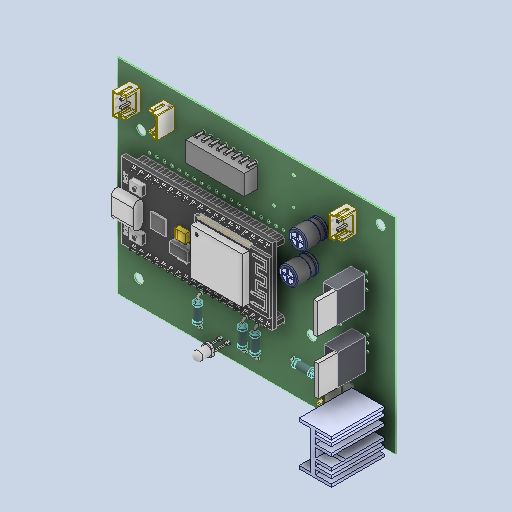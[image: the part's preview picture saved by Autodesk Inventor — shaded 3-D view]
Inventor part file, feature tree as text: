
AUTODESK INVENTOR PART (.ipt)
format: ipt  version: 2024 (Build 280153000, 153)  size: 6,783,488 bytes
history: native  units: in
note: dims shown in document units (in); Inventor stores cm internally (conversion verified against a paired STEP export)
features: other x145, extrude x53
ambient origin geometry x8: Origin, YZ Plane, XZ Plane, XY Plane, X Axis, Y Axis, Z Axis, Center Point
bodies: Solid1 (feature_tree), Solid2 (feature_tree), Solid3 (feature_tree), Solid4 (feature_tree), Solid5 (feature_tree), Solid6 (feature_tree), Solid7 (feature_tree), Solid8 (feature_tree), Solid9 (feature_tree), Solid10 (feature_tree), Solid11 (feature_tree), Solid12 (feature_tree), Solid13 (feature_tree), Solid14 (feature_tree), Solid15 (feature_tree), Solid16 (feature_tree), Solid17 (feature_tree), Solid18 (feature_tree), Solid19 (feature_tree), Solid20 (feature_tree), Solid21 (feature_tree), Solid22 (feature_tree), Solid23 (feature_tree), Solid24 (feature_tree), Solid25 (feature_tree), Solid26 (feature_tree), Solid27 (feature_tree), Solid28 (feature_tree), Solid29 (feature_tree), Solid30 (feature_tree), Solid31 (feature_tree), Solid32 (feature_tree), Solid33 (feature_tree), Solid34 (feature_tree), Solid35 (feature_tree), Solid36 (feature_tree), Solid37 (feature_tree), Solid38 (feature_tree), Solid39 (feature_tree), Solid40 (feature_tree), Solid41 (feature_tree), Solid42 (feature_tree), Solid43 (feature_tree), Solid44 (feature_tree), Solid45 (feature_tree), Solid46 (feature_tree), Solid47 (feature_tree), Solid48 (feature_tree), Solid49 (feature_tree), Solid50 (feature_tree), Solid51 (feature_tree), Solid52 (feature_tree), Solid53 (feature_tree), Solid54 (feature_tree), Solid55 (feature_tree), Solid56 (feature_tree), Solid57 (feature_tree), Solid58 (feature_tree), Solid59 (feature_tree), Solid60 (feature_tree), Solid61 (feature_tree), Solid62 (feature_tree), Solid63 (feature_tree), Solid64 (feature_tree), Solid65 (feature_tree), Solid66 (feature_tree), Solid67 (feature_tree), Solid68 (feature_tree), Solid69 (feature_tree), Solid70 (feature_tree), Solid71 (feature_tree), Solid72 (feature_tree), Solid73 (feature_tree), Solid74 (feature_tree), Solid75 (feature_tree), Solid76 (feature_tree), Solid77 (feature_tree), Solid78 (feature_tree), Solid79 (feature_tree), Solid80 (feature_tree), Solid81 (feature_tree), Solid82 (feature_tree), Solid83 (feature_tree), Solid84 (feature_tree), Solid85 (feature_tree), Solid86 (feature_tree), Solid87 (feature_tree), Solid88 (feature_tree), Solid89 (feature_tree), Solid90 (feature_tree), Solid91 (feature_tree), Solid92 (feature_tree), Solid93 (feature_tree), Solid94 (feature_tree), Solid95 (feature_tree), Solid96 (feature_tree), Solid97 (feature_tree), Solid98 (feature_tree), Solid99 (feature_tree), Solid100 (feature_tree), Solid101 (feature_tree), Solid102 (feature_tree), Solid103 (feature_tree), Solid104 (feature_tree), Solid105 (feature_tree), Solid106 (feature_tree), Solid107 (feature_tree), Solid108 (feature_tree), Solid109 (feature_tree), Solid110 (feature_tree), Solid111 (feature_tree), Solid112 (feature_tree), Solid113 (feature_tree), Solid114 (feature_tree), Solid115 (feature_tree), Solid116 (feature_tree), Solid117 (feature_tree), Solid118 (feature_tree), Solid119 (feature_tree), Solid120 (feature_tree), Solid121 (feature_tree), Solid122 (feature_tree), Solid123 (feature_tree), Solid124 (feature_tree), Solid125 (feature_tree), Solid126 (feature_tree), Solid127 (feature_tree), Solid128 (feature_tree), Solid129 (feature_tree), Solid130 (feature_tree), Solid131 (feature_tree), Solid132 (feature_tree), Solid133 (feature_tree), Solid134 (feature_tree), Solid135 (feature_tree), Solid136 (feature_tree), Solid137 (feature_tree), Solid138 (feature_tree), Solid139 (feature_tree), Solid140 (feature_tree), Solid141 (feature_tree), Solid142 (feature_tree), Solid143 (feature_tree), Solid144 (feature_tree), Solid145 (feature_tree), Solid146 (feature_tree), Solid147 (feature_tree), Solid148 (feature_tree), Solid149 (feature_tree), Solid150 (feature_tree), Solid151 (feature_tree), Solid152 (feature_tree), Solid153 (feature_tree), Solid154 (feature_tree), Solid155 (feature_tree), Solid156 (feature_tree), Solid157 (feature_tree), Solid158 (feature_tree), Solid159 (feature_tree), Solid160 (feature_tree), Solid161 (feature_tree), Solid162 (feature_tree), Solid163 (feature_tree), Solid164 (feature_tree), Solid165 (feature_tree), Solid166 (feature_tree), Solid167 (feature_tree), Solid168 (feature_tree), Solid169 (feature_tree), Solid170 (feature_tree), Solid171 (feature_tree), Solid172 (feature_tree), Solid173 (feature_tree), Solid174 (feature_tree), Solid175 (feature_tree), Solid176 (feature_tree), Solid177 (feature_tree), Solid178 (feature_tree), Solid179 (feature_tree), Solid180 (feature_tree), Solid181 (feature_tree), Solid182 (feature_tree), Solid183 (feature_tree), Solid184 (feature_tree), Solid185 (feature_tree), Solid186 (feature_tree), Solid187 (feature_tree), Solid188 (feature_tree), Solid189 (feature_tree), Solid190 (feature_tree), Solid191 (feature_tree), Solid192 (feature_tree), Solid193 (feature_tree), Solid194 (feature_tree), Solid195 (feature_tree), Solid196 (feature_tree), Solid197 (feature_tree), Solid198 (feature_tree), Solid199 (feature_tree), Solid200 (feature_tree), Solid201 (feature_tree), Solid202 (feature_tree), Solid203 (feature_tree), Solid204 (feature_tree), Solid205 (feature_tree), Solid206 (feature_tree), Solid207 (feature_tree), Solid208 (feature_tree), Solid209 (feature_tree), Solid210 (feature_tree), Solid211 (feature_tree), Solid212 (feature_tree), Solid213 (feature_tree), Solid214 (feature_tree)
feature tree (198):
  other  "Open CASCADE STEP translator 7.5 1.1.1_1:1"
  extrude  "Extruded_3:1"  [1 undecoded]
  extrude  "Extruded_5:1"  [1 undecoded]
  extrude  "Extruded_7:1"  [1 undecoded]
  extrude  "Extruded_9:1"  [1 undecoded]
  extrude  "Extruded_5:2"  [1 undecoded]
  extrude  "Extruded_7:2"  [1 undecoded]
  extrude  "Extruded_9:2"  [1 undecoded]
  extrude  "Extruded_5:3"  [1 undecoded]
  extrude  "Extruded_7:3"  [1 undecoded]
  extrude  "Extruded_9:3"  [1 undecoded]
  extrude  "Extruded_5:4"  [1 undecoded]
  extrude  "Extruded_7:4"  [1 undecoded]
  extrude  "Extruded_9:4"  [1 undecoded]
  extrude  "Extruded_5:5"  [1 undecoded]
  extrude  "Extruded_7:5"  [1 undecoded]
  extrude  "Extruded_9:5"  [1 undecoded]
  extrude  "Extruded_5:6"  [1 undecoded]
  extrude  "Extruded_7:6"  [1 undecoded]
  extrude  "Extruded_9:6"  [1 undecoded]
  extrude  "Extruded_5:7"  [1 undecoded]
  extrude  "Extruded_7:7"  [1 undecoded]
  extrude  "Extruded_9:7"  [1 undecoded]
  extrude  "Extruded_5:8"  [1 undecoded]
  extrude  "Extruded_7:8"  [1 undecoded]
  extrude  "Extruded_9:8"  [1 undecoded]
  extrude  "Extruded_5:9"  [1 undecoded]
  extrude  "Extruded_7:9"  [1 undecoded]
  extrude  "Extruded_9:9"  [1 undecoded]
  extrude  "Extruded_5:10"  [1 undecoded]
  extrude  "Extruded_7:10"  [1 undecoded]
  extrude  "Extruded_9:10"  [1 undecoded]
  extrude  "Extruded_5:11"  [1 undecoded]
  extrude  "Extruded_7:11"  [1 undecoded]
  extrude  "Extruded_9:11"  [1 undecoded]
  extrude  "Extruded_5:12"  [1 undecoded]
  extrude  "Extruded_7:12"  [1 undecoded]
  extrude  "Extruded_9:12"  [1 undecoded]
  extrude  "Extruded_5:13"  [1 undecoded]
  extrude  "Extruded_7:13"  [1 undecoded]
  extrude  "Extruded_9:13"  [1 undecoded]
  extrude  "Extruded_5:14"  [1 undecoded]
  extrude  "Extruded_7:14"  [1 undecoded]
  extrude  "Extruded_9:14"  [1 undecoded]
  extrude  "Extruded_5:15"  [1 undecoded]
  extrude  "Extruded_7:15"  [1 undecoded]
  extrude  "Extruded_9:15"  [1 undecoded]
  extrude  "Extruded_5:16"  [1 undecoded]
  extrude  "Extruded_7:16"  [1 undecoded]
  extrude  "Extruded_9:16"  [1 undecoded]
  other  "LM7805_Heatsink_57:1"
  other  "NodeMCU-32S-USBC-38pin-Narrow_59:1"
  other  "NodeMCU-32S-USBC-38pin-Narrow_59:2"
  other  "NodeMCU-32S-USBC-38pin-Narrow_59:3"
  other  "NodeMCU-32S-USBC-38pin-Narrow_59:4"
  other  "NodeMCU-32S-USBC-38pin-Narrow_59:5"
  other  "NodeMCU-32S-USBC-38pin-Narrow_59:6"
  other  "NodeMCU-32S-USBC-38pin-Narrow_59:7"
  other  "NodeMCU-32S-USBC-38pin-Narrow_59:8"
  other  "NodeMCU-32S-USBC-38pin-Narrow_59:9"
  other  "NodeMCU-32S-USBC-38pin-Narrow_59:10"
  other  "NodeMCU-32S-USBC-38pin-Narrow_59:11"
  other  "NodeMCU-32S-USBC-38pin-Narrow_59:12"
  other  "NodeMCU-32S-USBC-38pin-Narrow_59:13"
  other  "NodeMCU-32S-USBC-38pin-Narrow_59:14"
  other  "NodeMCU-32S-USBC-38pin-Narrow_59:15"
  other  "NodeMCU-32S-USBC-38pin-Narrow_59:16"
  other  "NodeMCU-32S-USBC-38pin-Narrow_59:17"
  other  "NodeMCU-32S-USBC-38pin-Narrow_59:18"
  other  "NodeMCU-32S-USBC-38pin-Narrow_59:19"
  other  "NodeMCU-32S-USBC-38pin-Narrow_59:20"
  other  "NodeMCU-32S-USBC-38pin-Narrow_59:21"
  other  "NodeMCU-32S-USBC-38pin-Narrow_59:22"
  other  "NodeMCU-32S-USBC-38pin-Narrow_59:23"
  other  "NodeMCU-32S-USBC-38pin-Narrow_59:24"
  other  "NodeMCU-32S-USBC-38pin-Narrow_59:25"
  other  "NodeMCU-32S-USBC-38pin-Narrow_59:26"
  other  "NodeMCU-32S-USBC-38pin-Narrow_59:27"
  other  "NodeMCU-32S-USBC-38pin-Narrow_59:28"
  other  "NodeMCU-32S-USBC-38pin-Narrow_59:29"
  other  "NodeMCU-32S-USBC-38pin-Narrow_59:30"
  other  "NodeMCU-32S-USBC-38pin-Narrow_59:31"
  other  "NodeMCU-32S-USBC-38pin-Narrow_59:32"
  other  "NodeMCU-32S-USBC-38pin-Narrow_59:33"
  other  "NodeMCU-32S-USBC-38pin-Narrow_59:34"
  other  "NodeMCU-32S-USBC-38pin-Narrow_59:35"
  other  "NodeMCU-32S-USBC-38pin-Narrow_59:36"
  other  "NodeMCU-32S-USBC-38pin-Narrow_59:37"
  other  "NodeMCU-32S-USBC-38pin-Narrow_59:38"
  other  "NodeMCU-32S-USBC-38pin-Narrow_59:39"
  other  "NodeMCU-32S-USBC-38pin-Narrow_59:40"
  other  "NodeMCU-32S-USBC-38pin-Narrow_59:41"
  other  "NodeMCU-32S-USBC-38pin-Narrow_59:42"
  other  "NodeMCU-32S-USBC-38pin-Narrow_59:43"
  other  "NodeMCU-32S-USBC-38pin-Narrow_59:44"
  other  "NodeMCU-32S-USBC-38pin-Narrow_59:45"
  other  "NodeMCU-32S-USBC-38pin-Narrow_59:46"
  other  "NodeMCU-32S-USBC-38pin-Narrow_59:47"
  other  "NodeMCU-32S-USBC-38pin-Narrow_59:48"
  other  "NodeMCU-32S-USBC-38pin-Narrow_59:49"
  other  "Vishay_63:1"
  other  "Vishay_63:2"
  other  "Vishay_63:3"
  other  "Vishay_63:4"
  other  "Vishay_63:5"
  other  "Vishay_63:6"
  other  "Vishay_63:7"
  other  "Vishay_63:8"
  other  "Vishay_63:9"
  other  "Vishay_63:10"
  other  "Vishay_63:11"
  other  "Vishay_63:12"
  other  "Vishay_63:13"
  other  "Vishay_63:14"
  other  "Vishay_63:15"
  other  "Vishay_63:16"
  other  "Vishay_63:17"
  other  "Vishay_63:18"
  other  "Vishay_63:19"
  other  "Vishay_63:20"
  other  "Vishay_63:21"
  other  "Vishay_63:22"
  other  "Vishay_63:23"
  other  "Vishay_63:24"
  other  "Vishay_63:25"
  other  "Vishay_63:26"
  other  "Vishay_63:27"
  other  "Vishay_63:28"
  other  "Vishay_63:29"
  other  "Vishay_63:30"
  other  "Vishay_63:31"
  other  "Vishay_63:32"
  other  "Vishay_63:33"
  other  "Vishay_63:34"
  other  "Vishay_63:35"
  other  "Vishay_63:36"
  other  "Vishay_63:37"
  other  "Vishay_63:38"
  other  "Vishay_63:39"
  other  "Vishay_63:40"
  other  "Vishay_63:41"
  other  "Vishay_63:42"
  other  "Vishay_63:43"
  other  "Vishay_63:44"
  other  "Vishay_63:45"
  other  "Vishay_63:46"
  other  "Vishay_63:47"
  other  "Vishay_63:48"
  other  "Vishay_63:49"
  other  "Vishay_63:50"
  other  "Vishay_63:51"
  other  "Vishay_63:52"
  other  "Vishay_63:53"
  other  "Vishay_63:54"
  other  "Vishay_63:55"
  other  "Vishay_63:56"
  other  "Vishay_63:57"
  other  "Vishay_63:58"
  other  "Vishay_63:59"
  other  "Vishay_63:60"
  extrude  "Extruded_72:1"  [1 undecoded]
  extrude  "Extruded_74:1"  [1 undecoded]
  extrude  "Extruded_72:2"  [1 undecoded]
  extrude  "Extruded_74:2"  [1 undecoded]
  other  "B2B-EH-A_81:1"
  other  "JST Logo adjustable_83:1"
  other  "Part7_84:1"
  other  "Part7_84:2"
  other  "B2B-EH-A_81:2"
  other  "JST Logo adjustable_83:2"
  other  "Part7_84:3"
  other  "Part7_84:4"
  other  "B2B-EH-A_81:3"
  other  "JST Logo adjustable_83:3"
  other  "Part7_84:5"
  other  "Part7_84:6"
  other  "B2B-EH-A_81:4"
  other  "JST Logo adjustable_83:4"
  other  "Part7_84:7"
  other  "Part7_84:8"
  other  "Lead_93:1"
  other  "Body_94:1"
  other  "ring_95:1"
  other  "151033xxx_98:1"
  other  "Cap_Panasonic_ECEA1AKA101E_eec_100:1"
  other  "Cap_Panasonic_ECEA1AKA101E_eec_100:2"
  other  "Cap_Panasonic_ECEA1AKA101E_eec_100:3"
  other  "Cap_Panasonic_ECEA1AKA101E_eec_100:4"
  other  "Cap_Panasonic_ECEA1AKA101E_eec_100:5"
  other  "Cap_Panasonic_ECEA1AKA101E_eec_100:6"
  other  "Cap_Panasonic_ECEA1AKA101E_eec_100:7"
  other  "Cap_Panasonic_ECEA1AKA101E_eec_102:1"
  other  "Cap_Panasonic_ECEA1AKA101E_eec_102:2"
  other  "Cap_Panasonic_ECEA1AKA101E_eec_102:3"
  other  "Cap_Panasonic_ECEA1AKA101E_eec_102:4"
  other  "Cap_Panasonic_ECEA1AKA101E_eec_102:5"
  other  "Cap_Panasonic_ECEA1AKA101E_eec_102:6"
  other  "Cap_Panasonic_ECEA1AKA101E_eec_102:7"
note: 53 required parameter values undecoded (feature->parameter linkage not recoverable at this tier; creation-order binding heuristic only, values carry confidence <= 0.55)
